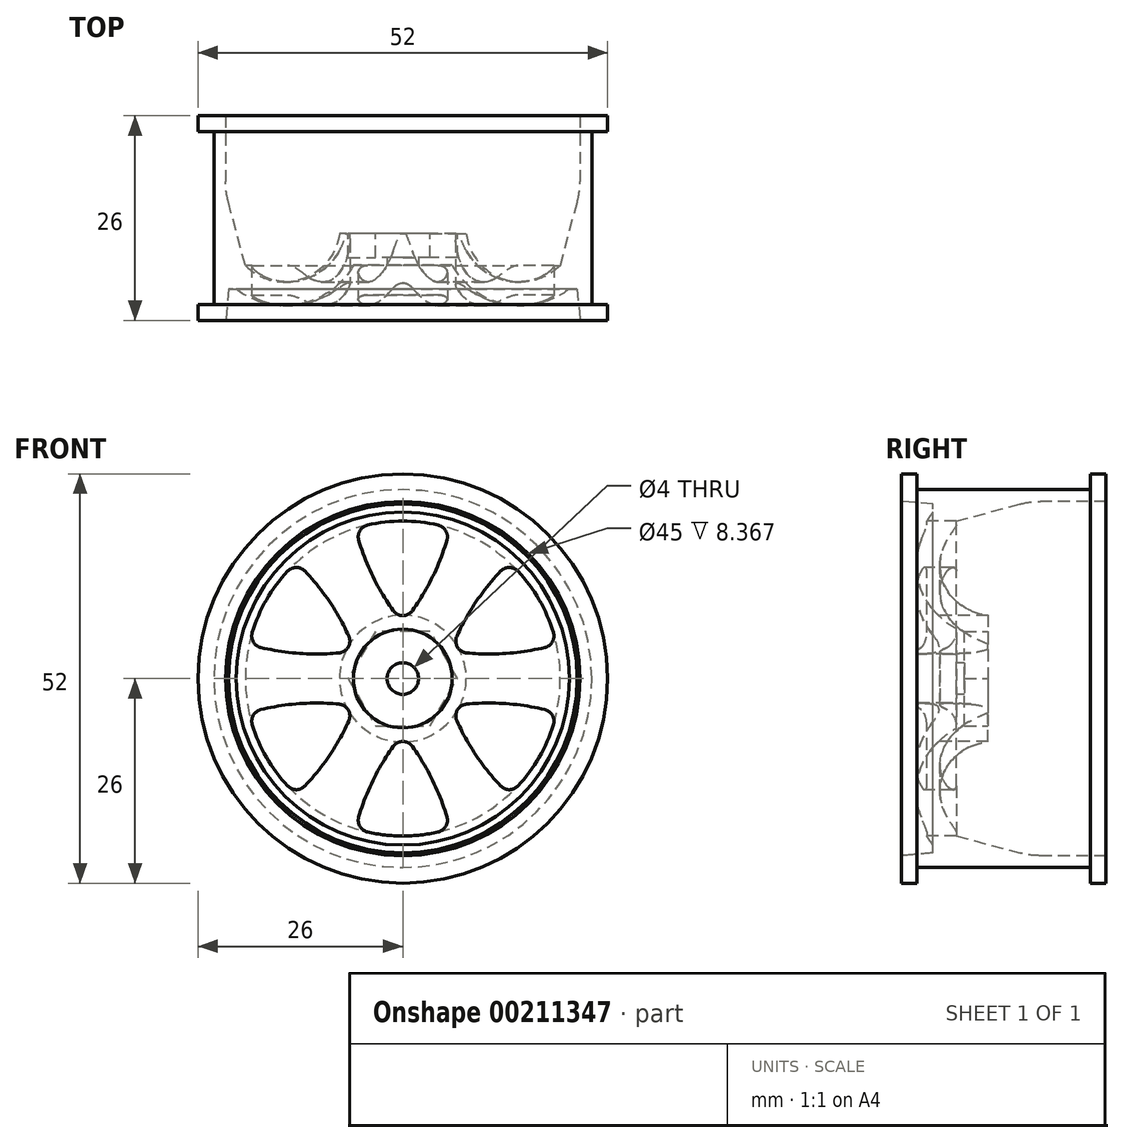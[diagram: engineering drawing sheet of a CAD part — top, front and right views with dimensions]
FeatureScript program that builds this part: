
annotation { "Feature Type Name" : "Feature", "Feature Type Description" : "" }
export const myFeature = defineFeature(function(context is Context, id is Id, definition is map)
    precondition{}
    {
        {
            var Q0;
            Q0=qCreatedBy(makeId("Right.planeOp"),FACE);
            var sketch = newSketch(context, id + "F0", { "sketchPlane" : qUnion([Q0])});
            skLineSegment(sketch, "E0", {"start": v(-23.3, 0) * mm, "end": v(25.67, 0) * mm, "construction": true});
            skLineSegment(sketch, "E1", {"start": v(-13, 26) * mm, "end": v(-13, 22.5) * mm});
            skLineSegment(sketch, "E2", {"start": v(-6, 6.27) * mm, "end": v(-6, 2) * mm});
            skLineSegment(sketch, "E3", {"start": v(-6, 2) * mm, "end": v(-2, 2) * mm});
            skLineSegment(sketch, "E4", {"start": v(-2, 2) * mm, "end": v(-2, 8.06) * mm});
            skLineSegment(sketch, "E5", {"start": v(-6.01, 20) * mm, "end": v(2.04, 22.16) * mm});
            skLineSegment(sketch, "E6", {"start": v(4.63, 22.5) * mm, "end": v(13, 22.5) * mm});
            skLineSegment(sketch, "E7", {"start": v(13, 22.5) * mm, "end": v(13, 26) * mm});
            skLineSegment(sketch, "E8", {"start": v(13, 26) * mm, "end": v(11, 26) * mm});
            skLineSegment(sketch, "E9", {"start": v(11, 26) * mm, "end": v(11, 24) * mm});
            skLineSegment(sketch, "E10", {"start": v(11, 24) * mm, "end": v(-11, 24) * mm});
            skLineSegment(sketch, "E11", {"start": v(-11, 24) * mm, "end": v(-11, 26) * mm});
            skLineSegment(sketch, "E12", {"start": v(-13, 26) * mm, "end": v(-11, 26) * mm});
            skLineSegment(sketch, "E13", {"start": v(0, 24) * mm, "end": v(0, 0) * mm, "construction": true});
            skLineSegment(sketch, "E14", {"start": v(-13, 22.5) * mm, "end": v(-9, 22.15) * mm});
            skLineSegment(sketch, "E15", {"start": v(-9, 22.15) * mm, "end": v(-9, 21.15) * mm});
            skArc(sketch, "E16", {"start": v(-9, 21.15) * mm, "mid": v(-10.92, 13.02) * mm, "end": v(-6, 6.27) * mm});
            skArc(sketch, "E17", {"start": v(-6.01, 20) * mm, "mid": v(-7.75, 12.77) * mm, "end": v(-2, 8.06) * mm});
            skPoint(sketch, "E18.visualSharp", {"position": v(3.32, 22.5) * mm});
            skArc(sketch, "E18.filletArc", {"start": v(4.63, 22.5) * mm, "mid": v(3.33, 22.41) * mm, "end": v(2.04, 22.16) * mm});
            skSolve(sketch);
        }
        {
            var Q0;
            Q0 = qSketchRegion(id + "F0", true);
            var Q1;
            Q1=sQuery(id+"F0.wireOp",EDGE,"E0");
            revolve(context, id + "F1", {"entities" : qUnion([Q0]), "axis" : qUnion([Q1]), "revolveType" : RevolveType.FULL});
        }
        {
            var Q0;
            Q0=makeQuery(id+"F1.opRevolve","SWEPT_FACE",FACE,{"disambiguationData":[OSD([sQuery(id+"F0.wireOp",EDGE,"E1")])]});
            var sketch = newSketch(context, id + "F2", { "sketchPlane" : qUnion([Q0])});
            skArc(sketch, "E19", {"start": v(4.5, 19.49) * mm, "mid": v(0, 20) * mm, "end": v(-4.5, 19.49) * mm});
            skArc(sketch, "E20", {"start": v(-1.22, 8.63) * mm, "mid": v(0, 8) * mm, "end": v(1.22, 8.63) * mm});
            skArc(sketch, "E21", {"start": v(-5.6, 17.6) * mm, "mid": v(-3.79, 12.93) * mm, "end": v(-1.22, 8.63) * mm});
            skLineSegment(sketch, "E22", {"start": v(0, 0) * mm, "end": v(0, 21) * mm, "construction": true});
            skArc(sketch, "E23.MirrorCS", {"start": v(5.6, 17.6) * mm, "mid": v(3.79, 12.93) * mm, "end": v(1.22, 8.63) * mm});
            skPoint(sketch, "E24.visualSharp", {"position": v(-6, 19.08) * mm});
            skArc(sketch, "E24.filletArc", {"start": v(-4.5, 19.49) * mm, "mid": v(-5.46, 18.78) * mm, "end": v(-5.6, 17.6) * mm});
            skArc(sketch, "E25.MirrorCS", {"start": v(4.5, 19.49) * mm, "mid": v(5.46, 18.78) * mm, "end": v(5.6, 17.6) * mm});
            skPoint(sketch, "E26.orphan", {"position": v(6, 19.08) * mm});
            skArc(sketch, "E27.1.0", {"start": v(-14.62, 13.64) * mm, "mid": v(-17.32, 10) * mm, "end": v(-19.13, 5.84) * mm});
            skArc(sketch, "E27.1.1", {"start": v(-19.13, 5.84) * mm, "mid": v(-19, 4.66) * mm, "end": v(-18.04, 3.95) * mm});
            skArc(sketch, "E27.1.2", {"start": v(-14.62, 13.64) * mm, "mid": v(-13.53, 14.12) * mm, "end": v(-12.44, 13.65) * mm});
            skArc(sketch, "E27.1.3", {"start": v(-12.44, 13.65) * mm, "mid": v(-9.3, 9.74) * mm, "end": v(-6.86, 5.37) * mm});
            skArc(sketch, "E27.1.4", {"start": v(-8.08, 3.26) * mm, "mid": v(-6.93, 4) * mm, "end": v(-6.86, 5.37) * mm});
            skArc(sketch, "E27.1.5", {"start": v(-18.04, 3.95) * mm, "mid": v(-13.1, 3.18) * mm, "end": v(-8.08, 3.26) * mm});
            skArc(sketch, "E27.2.0", {"start": v(-19.13, -5.84) * mm, "mid": v(-17.32, -10) * mm, "end": v(-14.62, -13.64) * mm});
            skArc(sketch, "E27.2.1", {"start": v(-14.62, -13.64) * mm, "mid": v(-13.53, -14.12) * mm, "end": v(-12.44, -13.65) * mm});
            skArc(sketch, "E27.2.2", {"start": v(-19.13, -5.84) * mm, "mid": v(-19, -4.66) * mm, "end": v(-18.04, -3.95) * mm});
            skArc(sketch, "E27.2.3", {"start": v(-18.04, -3.95) * mm, "mid": v(-13.1, -3.18) * mm, "end": v(-8.08, -3.26) * mm});
            skArc(sketch, "E27.2.4", {"start": v(-6.86, -5.37) * mm, "mid": v(-6.93, -4) * mm, "end": v(-8.08, -3.26) * mm});
            skArc(sketch, "E27.2.5", {"start": v(-12.44, -13.65) * mm, "mid": v(-9.3, -9.74) * mm, "end": v(-6.86, -5.37) * mm});
            skArc(sketch, "E27.3.0", {"start": v(-4.5, -19.49) * mm, "mid": v(0, -20) * mm, "end": v(4.5, -19.49) * mm});
            skArc(sketch, "E27.3.1", {"start": v(4.5, -19.49) * mm, "mid": v(5.46, -18.78) * mm, "end": v(5.6, -17.6) * mm});
            skArc(sketch, "E27.3.2", {"start": v(-4.5, -19.49) * mm, "mid": v(-5.46, -18.78) * mm, "end": v(-5.6, -17.6) * mm});
            skArc(sketch, "E27.3.3", {"start": v(-5.6, -17.6) * mm, "mid": v(-3.79, -12.93) * mm, "end": v(-1.22, -8.63) * mm});
            skArc(sketch, "E27.3.4", {"start": v(1.22, -8.63) * mm, "mid": v(0, -8) * mm, "end": v(-1.22, -8.63) * mm});
            skArc(sketch, "E27.3.5", {"start": v(5.6, -17.6) * mm, "mid": v(3.79, -12.93) * mm, "end": v(1.22, -8.63) * mm});
            skArc(sketch, "E27.4.0", {"start": v(14.62, -13.64) * mm, "mid": v(17.32, -10) * mm, "end": v(19.13, -5.84) * mm});
            skArc(sketch, "E27.4.1", {"start": v(19.13, -5.84) * mm, "mid": v(19, -4.66) * mm, "end": v(18.04, -3.95) * mm});
            skArc(sketch, "E27.4.2", {"start": v(14.62, -13.64) * mm, "mid": v(13.53, -14.12) * mm, "end": v(12.44, -13.65) * mm});
            skArc(sketch, "E27.4.3", {"start": v(12.44, -13.65) * mm, "mid": v(9.3, -9.74) * mm, "end": v(6.86, -5.37) * mm});
            skArc(sketch, "E27.4.4", {"start": v(8.08, -3.26) * mm, "mid": v(6.93, -4) * mm, "end": v(6.86, -5.37) * mm});
            skArc(sketch, "E27.4.5", {"start": v(18.04, -3.95) * mm, "mid": v(13.1, -3.18) * mm, "end": v(8.08, -3.26) * mm});
            skArc(sketch, "E27.5.0", {"start": v(19.13, 5.84) * mm, "mid": v(17.32, 10) * mm, "end": v(14.62, 13.64) * mm});
            skArc(sketch, "E27.5.1", {"start": v(14.62, 13.64) * mm, "mid": v(13.53, 14.12) * mm, "end": v(12.44, 13.65) * mm});
            skArc(sketch, "E27.5.2", {"start": v(19.13, 5.84) * mm, "mid": v(19, 4.66) * mm, "end": v(18.04, 3.95) * mm});
            skArc(sketch, "E27.5.3", {"start": v(18.04, 3.95) * mm, "mid": v(13.1, 3.18) * mm, "end": v(8.08, 3.26) * mm});
            skArc(sketch, "E27.5.4", {"start": v(6.86, 5.37) * mm, "mid": v(6.93, 4) * mm, "end": v(8.08, 3.26) * mm});
            skArc(sketch, "E27.5.5", {"start": v(12.44, 13.65) * mm, "mid": v(9.3, 9.74) * mm, "end": v(6.86, 5.37) * mm});
            skSolve(sketch);
        }
        {
            var Q0;
            Q0 = qSketchRegion(id + "F2", true);
            extrude(context, id + "F3", {"entities" : qUnion([Q0]), "operationType" : NewBodyOperationType.REMOVE, "oppositeDirection" : true, "depth" : 25 * mm});
        }
        {
            var Q0;
            Q0=makeQuery(id+"F1.opRevolve","SWEPT_FACE",FACE,{"disambiguationData":[OSD([sQuery(id+"F0.wireOp",EDGE,"E4")])]});
            var sketch = newSketch(context, id + "F4", { "sketchPlane" : qUnion([Q0])});
            skCircle(sketch, "E28.cCircle", {"center": v(0, 0) * mm, "radius": 6 * mm, "construction": true});
            skLineSegment(sketch, "E28.0", {"start": v(-3.46, 6) * mm, "end": v(3.46, 6) * mm});
            skLineSegment(sketch, "E28.1", {"start": v(3.46, 6) * mm, "end": v(6.93, 0) * mm});
            skLineSegment(sketch, "E28.2", {"start": v(6.93, 0) * mm, "end": v(3.46, -6) * mm});
            skLineSegment(sketch, "E28.3", {"start": v(3.46, -6) * mm, "end": v(-3.46, -6) * mm});
            skLineSegment(sketch, "E28.4", {"start": v(-3.46, -6) * mm, "end": v(-6.93, 0) * mm});
            skLineSegment(sketch, "E28.5", {"start": v(-6.93, 0) * mm, "end": v(-3.46, 6) * mm});
            skPoint(sketch, "E28.0.midPoint", {"position": v(0, 6) * mm});
            skSolve(sketch);
        }
        {
            var Q0;
            Q0 = qSketchRegion(id + "F4", true);
            extrude(context, id + "F5", {"entities" : qUnion([Q0]), "operationType" : NewBodyOperationType.REMOVE, "oppositeDirection" : true, "depth" : 3 * mm});
        }
    });
